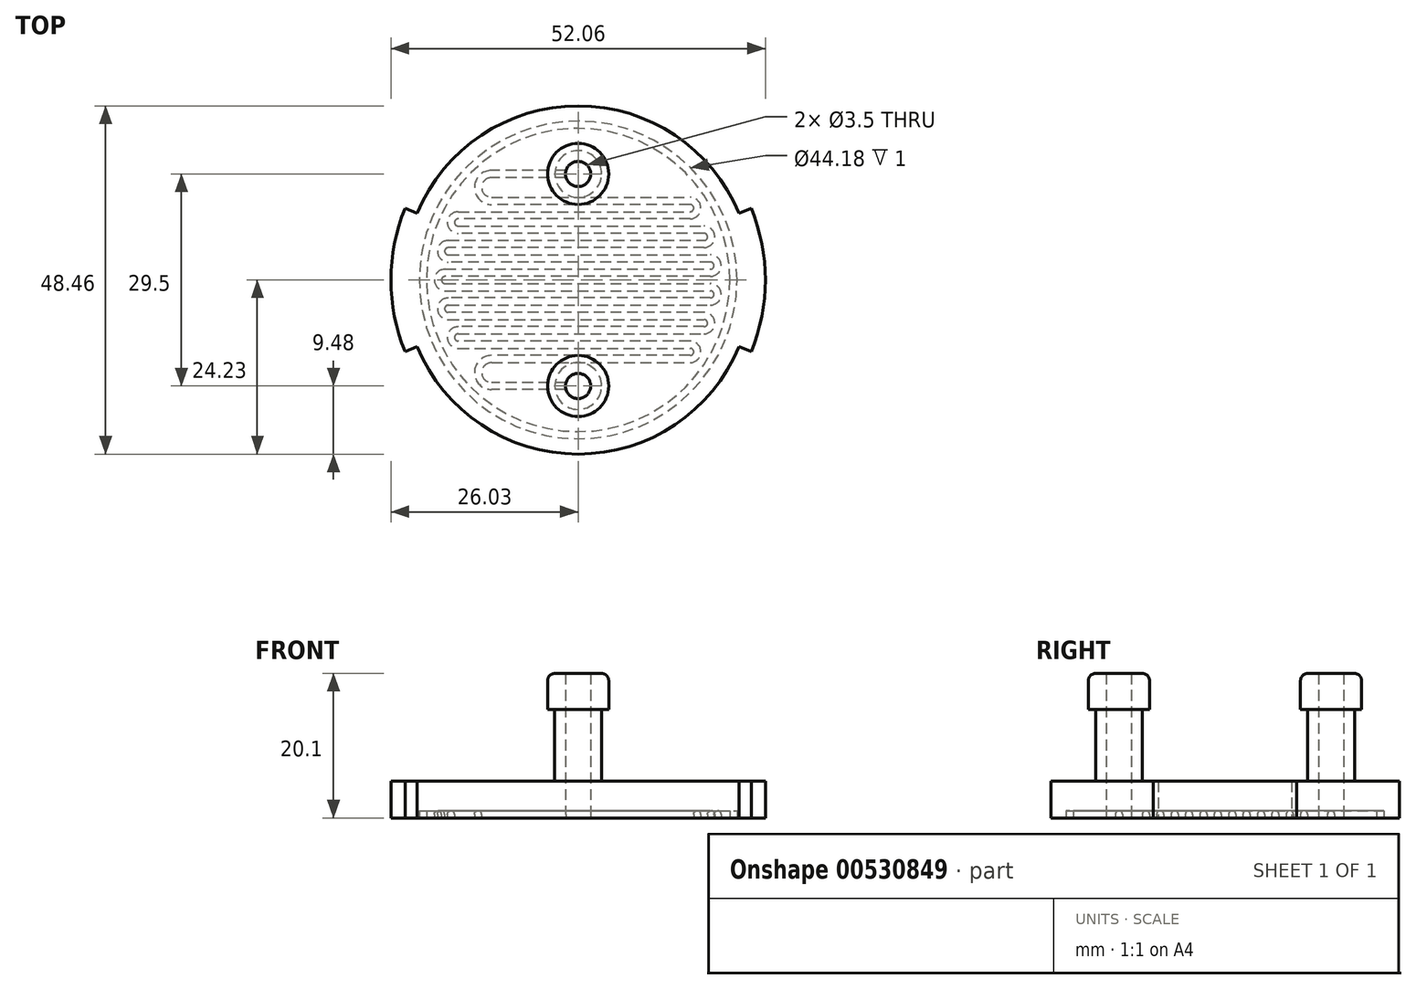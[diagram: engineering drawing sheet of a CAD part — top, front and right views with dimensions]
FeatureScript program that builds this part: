
annotation { "Feature Type Name" : "Feature", "Feature Type Description" : "" }
export const myFeature = defineFeature(function(context is Context, id is Id, definition is map)
    precondition{}
    {
        {
            var Q0;
            Q0=qCreatedBy(makeId("Top.planeOp"),FACE);
            var sketch = newSketch(context, id + "F0", { "sketchPlane" : qUnion([Q0])});
            skCircle(sketch, "E0", {"center": v(0, 0) * mm, "radius": 24.23 * mm});
            skSolve(sketch);
        }
        {
            var Q0;
            Q0 = qSketchRegion(id + "F0", true);
            extrude(context, id + "F1", {"entities" : qUnion([Q0]), "depth" : 5.1 * mm, "offsetDistance" : 25 * mm});
        }
        {
            var Q0;
            Q0=makeQuery(id+"F1.opExtrude","CAP_FACE",FACE,{"disambiguationData":[OSD([sQuery(id+"F0.wireOp",EDGE,"E0")])],"isStart":true});
            var sketch = newSketch(context, id + "F2", { "sketchPlane" : qUnion([Q0])});
            skCircle(sketch, "E1", {"center": v(0, 0) * mm, "radius": 22.1 * mm});
            skCircle(sketch, "E2", {"center": v(0, 0) * mm, "radius": 21.09 * mm});
            skSolve(sketch);
        }
        {
            var Q0;
            Q0 = qSketchRegion(id + "F2", true);
            extrude(context, id + "F3", {"entities" : qUnion([Q0]), "operationType" : NewBodyOperationType.REMOVE, "oppositeDirection" : true, "depth" : 1 * mm, "offsetDistance" : 25 * mm});
        }
        {
            var Q0;
            Q0=makeQuery(id+"F3.boolean.opBoolean","SPLIT",FACE,{"disambiguationData":[TD([makeQuery(id+"F3.opExtrude","SWEPT_FACE",FACE,{"disambiguationData":[OSD([sQuery(id+"F2.wireOp",EDGE,"E2")])]})])],"derivedFrom":makeQuery(id+"F1.opExtrude","CAP_FACE",FACE,{"disambiguationData":[OSD([sQuery(id+"F0.wireOp",EDGE,"E0")])],"isStart":true})});
            var sketch = newSketch(context, id + "F4", { "sketchPlane" : qUnion([Q0])});
            skCircle(sketch, "E3", {"center": v(0, 0) * mm, "radius": 20 * mm, "construction": true});
            skArc(sketch, "E4", {"start": v(-1.68, -15.25) * mm, "mid": v(1.75, -14.75) * mm, "end": v(-1.68, -14.25) * mm});
            skLineSegment(sketch, "E5", {"start": v(-1.68, -15.25) * mm, "end": v(-12.04, -15.25) * mm});
            skLineSegment(sketch, "E6", {"start": v(-1.68, -14.25) * mm, "end": v(-12.04, -14.25) * mm});
            skLineSegment(sketch, "E7", {"start": v(-12.04, -11.5) * mm, "end": v(15.56, -11.5) * mm});
            skLineSegment(sketch, "E8", {"start": v(15.56, -10.5) * mm, "end": v(-12.04, -10.5) * mm});
            skArc(sketch, "E9", {"start": v(-12.04, -15.25) * mm, "mid": v(-14.41, -12.88) * mm, "end": v(-12.04, -10.5) * mm});
            skArc(sketch, "E10", {"start": v(-12.04, -14.25) * mm, "mid": v(-13.41, -12.88) * mm, "end": v(-12.04, -11.5) * mm});
            skLineSegment(sketch, "E11.0.1.0", {"start": v(15.56, -8.5) * mm, "end": v(-16.68, -8.5) * mm});
            skLineSegment(sketch, "E11.0.1.1", {"start": v(-16.68, -9.5) * mm, "end": v(15.56, -9.5) * mm});
            skLineSegment(sketch, "E11.0.2.0", {"start": v(17.5, -6.5) * mm, "end": v(-16.68, -6.5) * mm});
            skLineSegment(sketch, "E11.0.2.1", {"start": v(-16.68, -7.5) * mm, "end": v(17.5, -7.5) * mm});
            skLineSegment(sketch, "E11.0.3.0", {"start": v(17.5, -4.5) * mm, "end": v(-18.06, -4.5) * mm});
            skLineSegment(sketch, "E11.0.3.1", {"start": v(-18.06, -5.5) * mm, "end": v(17.5, -5.5) * mm});
            skLineSegment(sketch, "E11.0.4.0", {"start": v(18.4, -2.5) * mm, "end": v(-18.06, -2.5) * mm});
            skLineSegment(sketch, "E11.0.4.1", {"start": v(-18.06, -3.5) * mm, "end": v(18.4, -3.5) * mm});
            skLineSegment(sketch, "E11.0.5.0", {"start": v(18.4, -0.5) * mm, "end": v(-18.5, -0.5) * mm});
            skLineSegment(sketch, "E11.0.5.1", {"start": v(-18.5, -1.5) * mm, "end": v(18.4, -1.5) * mm});
            skArc(sketch, "E12", {"start": v(15.56, -10.5) * mm, "mid": v(16.06, -10) * mm, "end": v(15.56, -9.5) * mm});
            skArc(sketch, "E13", {"start": v(15.56, -11.5) * mm, "mid": v(17.06, -10) * mm, "end": v(15.56, -8.5) * mm});
            skArc(sketch, "E14", {"start": v(-16.68, -9.5) * mm, "mid": v(-18.18, -8) * mm, "end": v(-16.68, -6.5) * mm});
            skArc(sketch, "E15", {"start": v(-16.68, -8.5) * mm, "mid": v(-17.18, -8) * mm, "end": v(-16.68, -7.5) * mm});
            skArc(sketch, "E16", {"start": v(17.5, -7.5) * mm, "mid": v(19, -6) * mm, "end": v(17.5, -4.5) * mm});
            skArc(sketch, "E17", {"start": v(17.5, -6.5) * mm, "mid": v(18, -6) * mm, "end": v(17.5, -5.5) * mm});
            skArc(sketch, "E18", {"start": v(-18.06, -5.5) * mm, "mid": v(-19.56, -4) * mm, "end": v(-18.06, -2.5) * mm});
            skArc(sketch, "E19", {"start": v(-18.06, -4.5) * mm, "mid": v(-18.56, -4) * mm, "end": v(-18.06, -3.5) * mm});
            skArc(sketch, "E20", {"start": v(18.4, -3.5) * mm, "mid": v(19.9, -2) * mm, "end": v(18.4, -0.5) * mm});
            skArc(sketch, "E21", {"start": v(18.4, -2.5) * mm, "mid": v(18.9, -2) * mm, "end": v(18.4, -1.5) * mm});
            skArc(sketch, "E22.MirrorCS", {"start": v(-16.68, 8.5) * mm, "mid": v(-17.18, 8) * mm, "end": v(-16.68, 7.5) * mm});
            skArc(sketch, "E23.MirrorCS", {"start": v(17.5, 6.5) * mm, "mid": v(18, 6) * mm, "end": v(17.5, 5.5) * mm});
            skLineSegment(sketch, "E24.MirrorCS", {"start": v(-12.04, 11.5) * mm, "end": v(15.56, 11.5) * mm});
            skArc(sketch, "E25.MirrorCS", {"start": v(-18.06, 5.5) * mm, "mid": v(-19.56, 4) * mm, "end": v(-18.06, 2.5) * mm});
            skLineSegment(sketch, "E26.MirrorCS", {"start": v(-1.68, 14.25) * mm, "end": v(-12.04, 14.25) * mm});
            skLineSegment(sketch, "E27.MirrorCS", {"start": v(-18.5, 1.5) * mm, "end": v(18.4, 1.5) * mm});
            skLineSegment(sketch, "E28.MirrorCS", {"start": v(-16.68, 9.5) * mm, "end": v(15.56, 9.5) * mm});
            skLineSegment(sketch, "E29.MirrorCS", {"start": v(-16.68, 7.5) * mm, "end": v(17.5, 7.5) * mm});
            skArc(sketch, "E30.MirrorCS", {"start": v(15.56, 11.5) * mm, "mid": v(17.06, 10) * mm, "end": v(15.56, 8.5) * mm});
            skArc(sketch, "E31.MirrorCS", {"start": v(-16.68, 9.5) * mm, "mid": v(-18.18, 8) * mm, "end": v(-16.68, 6.5) * mm});
            skLineSegment(sketch, "E32.MirrorCS", {"start": v(17.5, 6.5) * mm, "end": v(-16.68, 6.5) * mm});
            skArc(sketch, "E33.MirrorCS", {"start": v(18.4, 2.5) * mm, "mid": v(18.9, 2) * mm, "end": v(18.4, 1.5) * mm});
            skLineSegment(sketch, "E34.MirrorCS", {"start": v(-18.06, 3.5) * mm, "end": v(18.4, 3.5) * mm});
            skLineSegment(sketch, "E35.MirrorCS", {"start": v(18.4, 2.5) * mm, "end": v(-18.06, 2.5) * mm});
            skLineSegment(sketch, "E36.MirrorCS", {"start": v(15.56, 8.5) * mm, "end": v(-16.68, 8.5) * mm});
            skArc(sketch, "E37.MirrorCS", {"start": v(15.56, 10.5) * mm, "mid": v(16.06, 10) * mm, "end": v(15.56, 9.5) * mm});
            skArc(sketch, "E38.MirrorCS", {"start": v(-12.04, 14.25) * mm, "mid": v(-13.41, 12.88) * mm, "end": v(-12.04, 11.5) * mm});
            skArc(sketch, "E39.MirrorCS", {"start": v(17.5, 7.5) * mm, "mid": v(19, 6) * mm, "end": v(17.5, 4.5) * mm});
            skArc(sketch, "E40.MirrorCS", {"start": v(18.4, 3.5) * mm, "mid": v(19.9, 2) * mm, "end": v(18.4, 0.5) * mm});
            skArc(sketch, "E41.MirrorC", {"start": v(-1.68, 15.25) * mm, "mid": v(1.75, 14.75) * mm, "end": v(-1.68, 14.25) * mm});
            skLineSegment(sketch, "E42.MirrorCS", {"start": v(17.5, 4.5) * mm, "end": v(-18.06, 4.5) * mm});
            skArc(sketch, "E43.MirrorCS", {"start": v(-12.04, 15.25) * mm, "mid": v(-14.41, 12.88) * mm, "end": v(-12.04, 10.5) * mm});
            skLineSegment(sketch, "E44.MirrorCS", {"start": v(15.56, 10.5) * mm, "end": v(-12.04, 10.5) * mm});
            skLineSegment(sketch, "E45.MirrorCS", {"start": v(-1.68, 15.25) * mm, "end": v(-12.04, 15.25) * mm});
            skLineSegment(sketch, "E46.MirrorCS", {"start": v(-18.06, 5.5) * mm, "end": v(17.5, 5.5) * mm});
            skArc(sketch, "E47.MirrorCS", {"start": v(-18.06, 4.5) * mm, "mid": v(-18.56, 4) * mm, "end": v(-18.06, 3.5) * mm});
            skLineSegment(sketch, "E48", {"start": v(-18.5, 0.5) * mm, "end": v(18.4, 0.5) * mm});
            skArc(sketch, "E49", {"start": v(-18.5, 1.5) * mm, "mid": v(-20, 0) * mm, "end": v(-18.5, -1.5) * mm});
            skArc(sketch, "E50", {"start": v(-18.5, 0.5) * mm, "mid": v(-19, 0) * mm, "end": v(-18.5, -0.5) * mm});
            skPoint(sketch, "E51.orphan", {"position": v(0, 15.25) * mm});
            skPoint(sketch, "E52.orphan", {"position": v(0, 14.25) * mm});
            skPoint(sketch, "E53.orphan", {"position": v(0, -14.25) * mm});
            skPoint(sketch, "E54.orphan", {"position": v(0, -15.25) * mm});
            skSolve(sketch);
        }
        {
            var Q0;
            Q0 = qSketchRegion(id + "F4", true);
            extrude(context, id + "F5", {"entities" : qUnion([Q0]), "operationType" : NewBodyOperationType.REMOVE, "oppositeDirection" : true, "depth" : 1 * mm, "offsetDistance" : 25 * mm});
        }
        {
            var Q0;
            Q0=makeQuery(id+"F5.boolean.opBoolean","COPY",FACE,{"derivedFrom":makeQuery(id+"F5.opExtrude","CAP_FACE",FACE,{"disambiguationData":[OSD([sQuery(id+"F4.wireOp",EDGE,"E4"),sQuery(id+"F4.wireOp",EDGE,"E5"),sQuery(id+"F4.wireOp",EDGE,"E6"),sQuery(id+"F4.wireOp",EDGE,"E7"),sQuery(id+"F4.wireOp",EDGE,"E8"),sQuery(id+"F4.wireOp",EDGE,"E9"),sQuery(id+"F4.wireOp",EDGE,"E10"),sQuery(id+"F4.wireOp",EDGE,"E11.0.1.0"),sQuery(id+"F4.wireOp",EDGE,"E11.0.1.1"),sQuery(id+"F4.wireOp",EDGE,"E11.0.2.0"),sQuery(id+"F4.wireOp",EDGE,"E11.0.2.1"),sQuery(id+"F4.wireOp",EDGE,"E11.0.3.0"),sQuery(id+"F4.wireOp",EDGE,"E11.0.3.1"),sQuery(id+"F4.wireOp",EDGE,"E11.0.4.0"),sQuery(id+"F4.wireOp",EDGE,"E11.0.4.1"),sQuery(id+"F4.wireOp",EDGE,"E11.0.5.0"),sQuery(id+"F4.wireOp",EDGE,"E11.0.5.1"),sQuery(id+"F4.wireOp",EDGE,"E12"),sQuery(id+"F4.wireOp",EDGE,"E13"),sQuery(id+"F4.wireOp",EDGE,"E14"),sQuery(id+"F4.wireOp",EDGE,"E15"),sQuery(id+"F4.wireOp",EDGE,"E16"),sQuery(id+"F4.wireOp",EDGE,"E17"),sQuery(id+"F4.wireOp",EDGE,"E18"),sQuery(id+"F4.wireOp",EDGE,"E19"),sQuery(id+"F4.wireOp",EDGE,"E20"),sQuery(id+"F4.wireOp",EDGE,"E21"),sQuery(id+"F4.wireOp",EDGE,"E22.MirrorCS"),sQuery(id+"F4.wireOp",EDGE,"E23.MirrorCS"),sQuery(id+"F4.wireOp",EDGE,"E24.MirrorCS"),sQuery(id+"F4.wireOp",EDGE,"E25.MirrorCS"),sQuery(id+"F4.wireOp",EDGE,"E26.MirrorCS"),sQuery(id+"F4.wireOp",EDGE,"E27.MirrorCS"),sQuery(id+"F4.wireOp",EDGE,"E28.MirrorCS"),sQuery(id+"F4.wireOp",EDGE,"E29.MirrorCS"),sQuery(id+"F4.wireOp",EDGE,"E30.MirrorCS"),sQuery(id+"F4.wireOp",EDGE,"E31.MirrorCS"),sQuery(id+"F4.wireOp",EDGE,"E32.MirrorCS"),sQuery(id+"F4.wireOp",EDGE,"E33.MirrorCS"),sQuery(id+"F4.wireOp",EDGE,"E34.MirrorCS"),sQuery(id+"F4.wireOp",EDGE,"E35.MirrorCS"),sQuery(id+"F4.wireOp",EDGE,"E36.MirrorCS"),sQuery(id+"F4.wireOp",EDGE,"E37.MirrorCS"),sQuery(id+"F4.wireOp",EDGE,"E38.MirrorCS"),sQuery(id+"F4.wireOp",EDGE,"E39.MirrorCS"),sQuery(id+"F4.wireOp",EDGE,"E40.MirrorCS"),sQuery(id+"F4.wireOp",EDGE,"E41.MirrorC"),sQuery(id+"F4.wireOp",EDGE,"E42.MirrorCS"),sQuery(id+"F4.wireOp",EDGE,"E43.MirrorCS"),sQuery(id+"F4.wireOp",EDGE,"E44.MirrorCS"),sQuery(id+"F4.wireOp",EDGE,"E45.MirrorCS"),sQuery(id+"F4.wireOp",EDGE,"E46.MirrorCS"),sQuery(id+"F4.wireOp",EDGE,"E47.MirrorCS"),sQuery(id+"F4.wireOp",EDGE,"E48"),sQuery(id+"F4.wireOp",EDGE,"E49"),sQuery(id+"F4.wireOp",EDGE,"E50")])],"isStart":false})});
            fillet(context, id + "F6", {"entities" : qUnion([Q0]), "radius" : 0.5 * mm, "tangentPropagation" : true, "allowEdgeOverflow" : false});
        }
        {
            var Q0;
            Q0=makeQuery(id+"F3.boolean.opBoolean","SPLIT",FACE,{"disambiguationData":[TD([makeQuery(id+"F3.opExtrude","SWEPT_FACE",FACE,{"disambiguationData":[OSD([sQuery(id+"F2.wireOp",EDGE,"E2")])]})])],"derivedFrom":makeQuery(id+"F1.opExtrude","CAP_FACE",FACE,{"disambiguationData":[OSD([sQuery(id+"F0.wireOp",EDGE,"E0")])],"isStart":true})});
            var sketch = newSketch(context, id + "F7", { "sketchPlane" : qUnion([Q0])});
            skArc(sketch, "E55.0", {"start": v(-1.68, 15.25) * mm, "mid": v(1.75, 14.75) * mm, "end": v(-1.68, 14.25) * mm});
            skArc(sketch, "E56.0", {"start": v(-1.68, -15.25) * mm, "mid": v(1.75, -14.75) * mm, "end": v(-1.68, -14.25) * mm});
            skArc(sketch, "E57", {"start": v(-1.68, 15.25) * mm, "mid": v(-1.75, 14.75) * mm, "end": v(-1.68, 14.25) * mm});
            skArc(sketch, "E58", {"start": v(-1.68, -14.25) * mm, "mid": v(-1.75, -14.75) * mm, "end": v(-1.68, -15.25) * mm});
            skSolve(sketch);
        }
        {
            var Q0;
            Q0 = qSketchRegion(id + "F7", true);
            extrude(context, id + "F8", {"entities" : qUnion([Q0]), "operationType" : NewBodyOperationType.REMOVE, "endBound" : BoundingType.THROUGH_ALL, "oppositeDirection" : true, "depth" : 25 * mm, "offsetDistance" : 25 * mm});
        }
        {
            var Q0;
            Q0=makeQuery(id+"F1.opExtrude","CAP_FACE",FACE,{"disambiguationData":[OSD([sQuery(id+"F0.wireOp",EDGE,"E0")])],"isStart":false});
            var sketch = newSketch(context, id + "F9", { "sketchPlane" : qUnion([Q0])});
            skCircle(sketch, "E59.0", {"center": v(0, 14.75) * mm, "radius": 1.75 * mm});
            skCircle(sketch, "E60.0", {"center": v(0, -14.75) * mm, "radius": 1.75 * mm});
            skCircle(sketch, "E61", {"center": v(0, 14.75) * mm, "radius": 3.25 * mm});
            skCircle(sketch, "E62", {"center": v(0, -14.75) * mm, "radius": 3.25 * mm});
            skSolve(sketch);
        }
        {
            var Q0;
            Q0 = qSketchRegion(id + "F9", true);
            extrude(context, id + "F10", {"entities" : qUnion([Q0]), "operationType" : NewBodyOperationType.ADD, "depth" : 15 * mm, "offsetDistance" : 25 * mm});
        }
        {
            var Q0;
            Q0=qCreatedBy(makeId("Top.planeOp"),FACE);
            var sketch = newSketch(context, id + "F11", { "sketchPlane" : qUnion([Q0])});
            skArc(sketch, "E63", {"start": v(-24.06, 9.94) * mm, "mid": v(-26.04, 0) * mm, "end": v(-24.06, -9.95) * mm});
            skLineSegment(sketch, "E64", {"start": v(-24.06, 9.95) * mm, "end": v(24.06, 9.95) * mm, "construction": true});
            skLineSegment(sketch, "E65.MirrorCS", {"start": v(-24.06, -9.95) * mm, "end": v(24.06, -9.95) * mm, "construction": true});
            skLineSegment(sketch, "E66", {"start": v(-24.06, 9.95) * mm, "end": v(24.06, -9.95) * mm, "construction": true});
            skLineSegment(sketch, "E67", {"start": v(24.06, 9.95) * mm, "end": v(-24.06, -9.95) * mm, "construction": true});
            skArc(sketch, "E68.trimOffspring", {"start": v(24.06, -9.95) * mm, "mid": v(26.04, 0) * mm, "end": v(24.06, 9.95) * mm});
            skArc(sketch, "E69.0", {"start": v(-22.39, 9.26) * mm, "mid": v(-24.22, 0) * mm, "end": v(-22.39, -9.25) * mm});
            skArc(sketch, "E70.trimOffspring", {"start": v(22.39, -9.25) * mm, "mid": v(24.23, 0) * mm, "end": v(22.39, 9.25) * mm});
            skLineSegment(sketch, "E71", {"start": v(24.06, -9.95) * mm, "end": v(22.39, -9.25) * mm});
            skLineSegment(sketch, "E72", {"start": v(24.06, 9.95) * mm, "end": v(22.39, 9.25) * mm});
            skLineSegment(sketch, "E73", {"start": v(-24.06, -9.95) * mm, "end": v(-22.39, -9.25) * mm});
            skLineSegment(sketch, "E74", {"start": v(-24.06, 9.94) * mm, "end": v(-22.39, 9.26) * mm});
            skSolve(sketch);
        }
        {
            var Q0;
            Q0 = qSketchRegion(id + "F11", true);
            var Q1;
            Q1=makeQuery(id+"F1.opExtrude","CAP_FACE",FACE,{"disambiguationData":[OSD([sQuery(id+"F0.wireOp",EDGE,"E0")])],"isStart":false});
            extrude(context, id + "F12", {"entities" : qUnion([Q0]), "operationType" : NewBodyOperationType.ADD, "endBound" : BoundingType.UP_TO_SURFACE, "depth" : 25 * mm, "endBoundEntityFace" : qUnion([Q1]), "offsetDistance" : 25 * mm});
        }
        {
            var Q0;
            Q0=makeQuery(id+"F10.opExtrude","CAP_FACE",FACE,{"disambiguationData":[OSD([sQuery(id+"F9.wireOp",EDGE,"E59.0"),sQuery(id+"F9.wireOp",EDGE,"E61")])],"isStart":false});
            cPlane(context, id + "F13", {"entities" : qUnion([Q0]), "cplaneType" : CPlaneType.OFFSET, "offset" : 5 * mm, "oppositeDirection" : true, "width" : 150 * mm, "height" : 150 * mm});
        }
        {
            var Q0;
            Q0=qCreatedBy(id+"F13.planeOp",FACE);
            var sketch = newSketch(context, id + "F14", { "sketchPlane" : qUnion([Q0])});
            skCircle(sketch, "E75.0", {"center": v(0, 14.75) * mm, "radius": 3.25 * mm});
            skCircle(sketch, "E76.0", {"center": v(0, -14.75) * mm, "radius": 3.25 * mm});
            skCircle(sketch, "E77", {"center": v(0, 14.75) * mm, "radius": 4.25 * mm});
            skCircle(sketch, "E78", {"center": v(0, -14.75) * mm, "radius": 4.25 * mm});
            skSolve(sketch);
        }
        {
            var Q0;
            Q0 = qSketchRegion(id + "F14", true);
            var Q1;
            Q1=makeQuery(id+"F10.opExtrude","CAP_FACE",FACE,{"disambiguationData":[OSD([sQuery(id+"F9.wireOp",EDGE,"E59.0"),sQuery(id+"F9.wireOp",EDGE,"E61")])],"isStart":false});
            extrude(context, id + "F15", {"entities" : qUnion([Q0]), "operationType" : NewBodyOperationType.ADD, "endBound" : BoundingType.UP_TO_SURFACE, "depth" : 25 * mm, "endBoundEntityFace" : qUnion([Q1]), "offsetDistance" : 25 * mm});
        }
        {
            var Q0;
            Q0=makeQuery(id+"F15.opExtrude","CAP_EDGE",EDGE,{"disambiguationData":[OSD([sQuery(id+"F14.wireOp",EDGE,"E77")])],"isStart":false});
            var Q1;
            Q1=makeQuery(id+"F15.opExtrude","CAP_EDGE",EDGE,{"disambiguationData":[OSD([sQuery(id+"F14.wireOp",EDGE,"E78")])],"isStart":false});
            fillet(context, id + "F16", {"entities" : qUnion([Q0, Q1]), "radius" : 1 * mm, "tangentPropagation" : true, "allowEdgeOverflow" : false});
        }
    });
